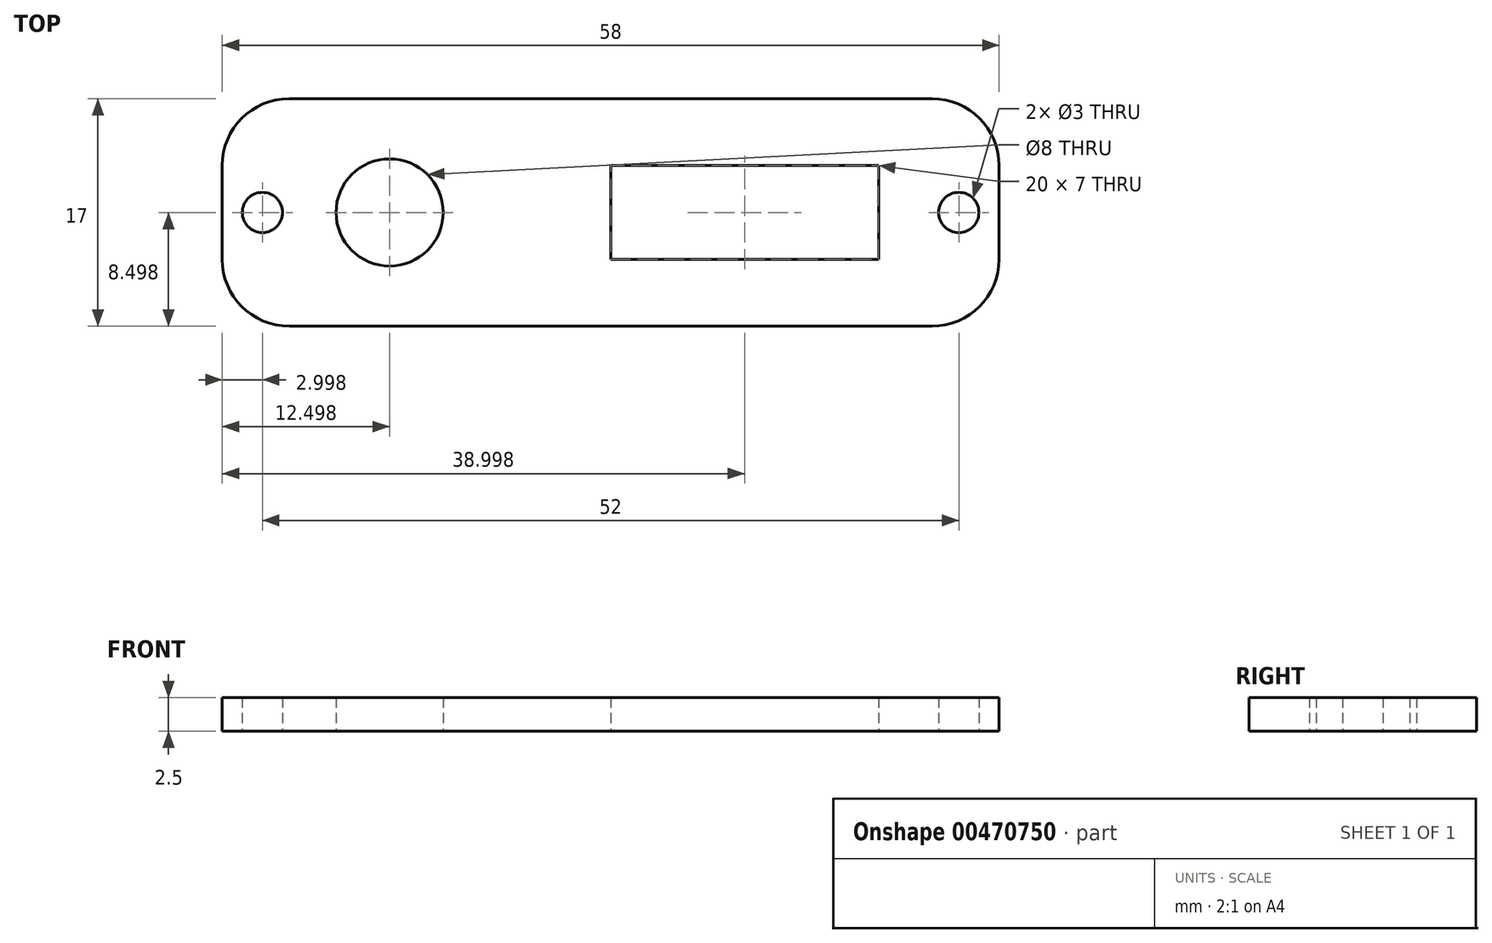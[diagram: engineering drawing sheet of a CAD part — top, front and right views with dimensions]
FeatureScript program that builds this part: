
annotation { "Feature Type Name" : "Feature", "Feature Type Description" : "" }
export const myFeature = defineFeature(function(context is Context, id is Id, definition is map)
    precondition{}
    {
        {
            var Q0;
            Q0=qCreatedBy(makeId("Top.planeOp"),FACE);
            var sketch = newSketch(context, id + "F0", { "sketchPlane" : qUnion([Q0])});
            skLineSegment(sketch, "E0.bottom", {"start": v(-25.36, -1.6) * mm, "end": v(32.64, -1.6) * mm});
            skLineSegment(sketch, "E0.top", {"start": v(-25.36, -18.6) * mm, "end": v(32.64, -18.6) * mm});
            skLineSegment(sketch, "E0.left", {"start": v(-25.36, -1.6) * mm, "end": v(-25.36, -18.6) * mm});
            skLineSegment(sketch, "E0.right", {"start": v(32.64, -1.6) * mm, "end": v(32.64, -18.6) * mm});
            skCircle(sketch, "E1", {"center": v(-12.86, -10.1) * mm, "radius": 4 * mm});
            skLineSegment(sketch, "E2.bottom", {"start": v(23.64, -13.6) * mm, "end": v(3.64, -13.6) * mm});
            skLineSegment(sketch, "E2.top", {"start": v(23.64, -6.6) * mm, "end": v(3.64, -6.6) * mm});
            skLineSegment(sketch, "E2.left", {"start": v(23.64, -13.6) * mm, "end": v(23.64, -6.6) * mm});
            skLineSegment(sketch, "E2.right", {"start": v(3.64, -13.6) * mm, "end": v(3.64, -6.6) * mm});
            skPoint(sketch, "E2.middle", {"position": v(13.64, -10.1) * mm});
            skCircle(sketch, "E3", {"center": v(-22.36, -10.1) * mm, "radius": 1.5 * mm});
            skCircle(sketch, "E4", {"center": v(29.64, -10.1) * mm, "radius": 1.5 * mm});
            skSolve(sketch);
        }
        {
            var Q0;
            Q0=makeQuery(id+"F0.imprint","IMPRINT",FACE,{"disambiguationData":[TD([[makeQuery(id+"F0.imprint","IMPRINT",EDGE,{"derivedFrom":sQuery(id+"F0.wireOp",EDGE,"E0.bottom")}),-1.0]])]});
            extrude(context, id + "F1", {"entities" : qUnion([Q0]), "depth" : 2.5 * mm, "offsetDistance" : 25 * mm});
        }
        {
            var Q0;
            Q0=makeQuery(id+"F1.opExtrude","SWEPT_EDGE",EDGE,{"disambiguationData":[OSD([sQuery(id+"F0.wireOp",EDGE,"E0.bottom"),sQuery(id+"F0.wireOp",EDGE,"E0.left")])]});
            var Q1;
            Q1=makeQuery(id+"F1.opExtrude","SWEPT_EDGE",EDGE,{"disambiguationData":[OSD([sQuery(id+"F0.wireOp",EDGE,"E0.bottom"),sQuery(id+"F0.wireOp",EDGE,"E0.right")])]});
            var Q2;
            Q2=makeQuery(id+"F1.opExtrude","SWEPT_EDGE",EDGE,{"disambiguationData":[OSD([sQuery(id+"F0.wireOp",EDGE,"E0.top"),sQuery(id+"F0.wireOp",EDGE,"E0.left")])]});
            var Q3;
            Q3=makeQuery(id+"F1.opExtrude","SWEPT_EDGE",EDGE,{"disambiguationData":[OSD([sQuery(id+"F0.wireOp",EDGE,"E0.top"),sQuery(id+"F0.wireOp",EDGE,"E0.right")])]});
            fillet(context, id + "F2", {"entities" : qUnion([Q0, Q1, Q2, Q3]), "tangentPropagation" : true, "radius" : 5 * mm, "defaultsChanged" : false, "vertexSettings" : [], "allowEdgeOverflow" : false});
        }
    });
